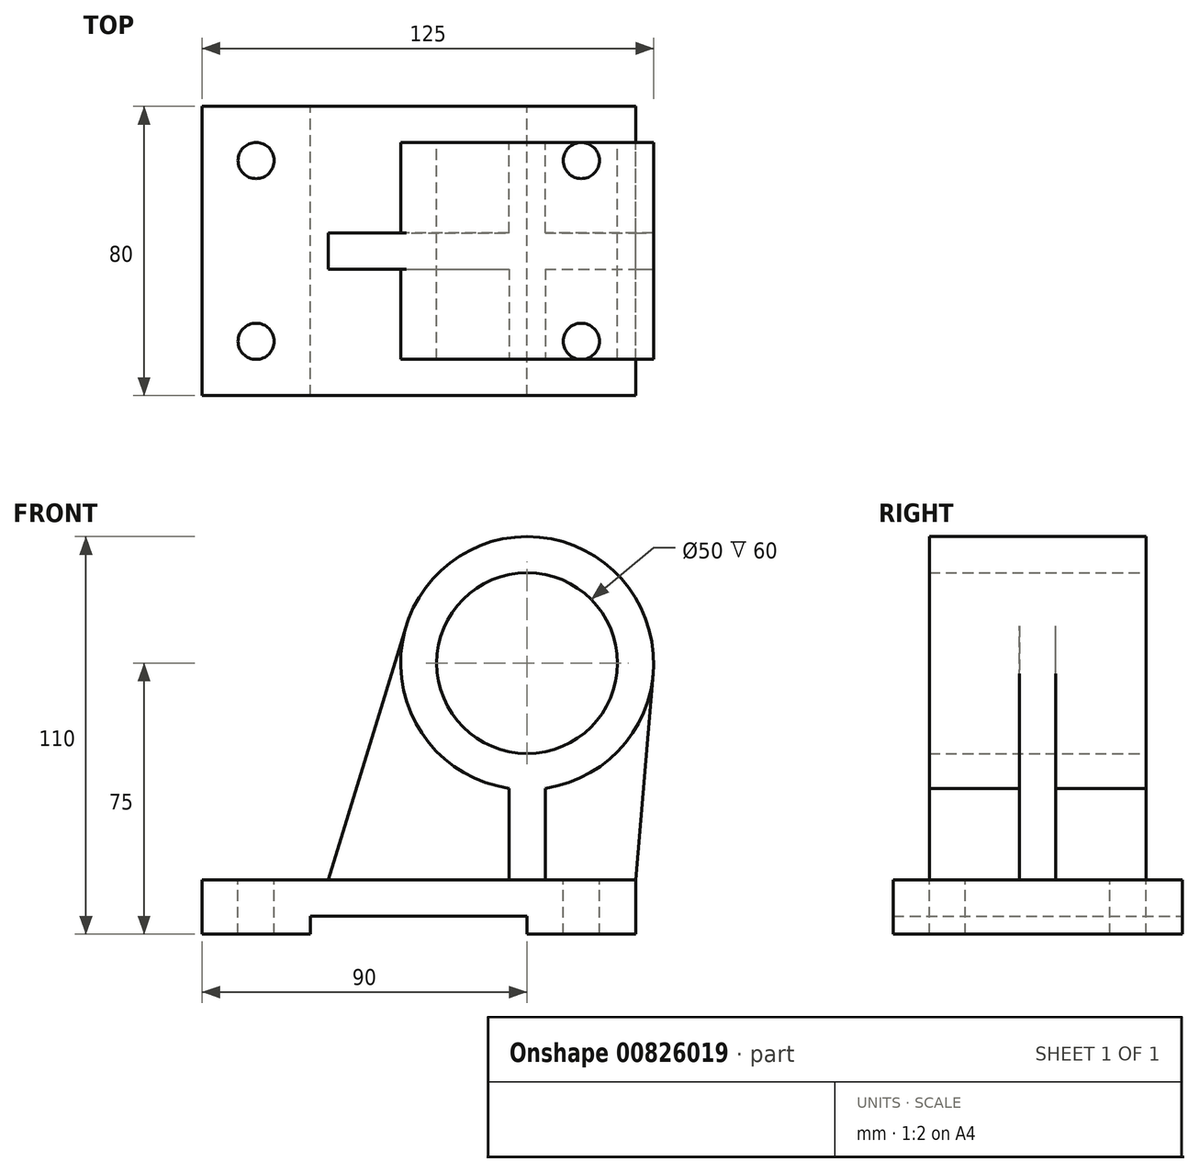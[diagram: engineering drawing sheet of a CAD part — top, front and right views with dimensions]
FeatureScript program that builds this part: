
annotation { "Feature Type Name" : "Feature", "Feature Type Description" : "" }
export const myFeature = defineFeature(function(context is Context, id is Id, definition is map)
    precondition{}
    {
        {
            var Q0;
            Q0=qCreatedBy(makeId("Front.planeOp"),FACE);
            var sketch = newSketch(context, id + "F0", { "sketchPlane" : qUnion([Q0])});
            skLineSegment(sketch, "E0", {"start": v(0, 0) * mm, "end": v(30, 0) * mm});
            skLineSegment(sketch, "E1", {"start": v(30, 0) * mm, "end": v(30, 5) * mm});
            skLineSegment(sketch, "E2", {"start": v(30, 5) * mm, "end": v(90, 5) * mm});
            skLineSegment(sketch, "E3", {"start": v(90, 5) * mm, "end": v(90, 0) * mm});
            skLineSegment(sketch, "E4", {"start": v(90, 0) * mm, "end": v(120, 0) * mm});
            skLineSegment(sketch, "E5", {"start": v(120, 0) * mm, "end": v(120, 15) * mm});
            skLineSegment(sketch, "E6", {"start": v(120, 15) * mm, "end": v(0, 15) * mm});
            skLineSegment(sketch, "E7", {"start": v(0, 15) * mm, "end": v(0, 0) * mm});
            skCircle(sketch, "E8", {"center": v(90, 75) * mm, "radius": 25 * mm});
            skCircle(sketch, "E9", {"center": v(90, 75) * mm, "radius": 35 * mm});
            skLineSegment(sketch, "E10", {"start": v(35, 15) * mm, "end": v(56.54, 85.26) * mm});
            skLineSegment(sketch, "E11", {"start": v(120, 15) * mm, "end": v(124.87, 72.02) * mm});
            skSolve(sketch);
        }
        {
            var Q0;
            Q0 = qSketchRegion(id + "F0", true);
            extrude(context, id + "F1", {"entities" : qUnion([Q0]), "endBound" : BoundingType.SYMMETRIC, "depth" : 80 * mm, "offsetDistance" : 25 * mm});
        }
        {
            var Q0;
            Q0=makeQuery(id+"F1.opExtrude","CAP_FACE",FACE,{"disambiguationData":[OSD([sQuery(id+"F0.wireOp",EDGE,"E0"),sQuery(id+"F0.wireOp",EDGE,"E1"),sQuery(id+"F0.wireOp",EDGE,"E2"),sQuery(id+"F0.wireOp",EDGE,"E3"),sQuery(id+"F0.wireOp",EDGE,"E4"),sQuery(id+"F0.wireOp",EDGE,"E5"),sQuery(id+"F0.wireOp",EDGE,"E6"),sQuery(id+"F0.wireOp",EDGE,"E7"),sQuery(id+"F0.wireOp",EDGE,"E8"),sQuery(id+"F0.wireOp",EDGE,"E9"),sQuery(id+"F0.wireOp",EDGE,"E10"),sQuery(id+"F0.wireOp",EDGE,"E11")])],"isStart":false});
            var sketch = newSketch(context, id + "F2", { "sketchPlane" : qUnion([Q0])});
            skLineSegment(sketch, "E12", {"start": v(35, 15) * mm, "end": v(120, 15) * mm});
            skSolve(sketch);
        }
        {
            var Q0;
            Q0=makeQuery(id+"F2.imprint","IMPRINT",FACE,{"disambiguationData":[TD([[makeQuery(id+"F2.imprint","IMPRINT",EDGE,{"derivedFrom":sQuery(id+"F2.wireOp",EDGE,"E12")}),1.0]])]});
            extrude(context, id + "F3", {"entities" : qUnion([Q0]), "operationType" : NewBodyOperationType.REMOVE, "oppositeDirection" : true, "depth" : 10 * mm, "offsetDistance" : 25 * mm});
        }
        {
            var Q0;
            Q0=makeQuery(id+"F1.opExtrude","CAP_FACE",FACE,{"disambiguationData":[OSD([sQuery(id+"F0.wireOp",EDGE,"E0"),sQuery(id+"F0.wireOp",EDGE,"E1"),sQuery(id+"F0.wireOp",EDGE,"E2"),sQuery(id+"F0.wireOp",EDGE,"E3"),sQuery(id+"F0.wireOp",EDGE,"E4"),sQuery(id+"F0.wireOp",EDGE,"E5"),sQuery(id+"F0.wireOp",EDGE,"E6"),sQuery(id+"F0.wireOp",EDGE,"E7"),sQuery(id+"F0.wireOp",EDGE,"E8"),sQuery(id+"F0.wireOp",EDGE,"E9"),sQuery(id+"F0.wireOp",EDGE,"E10"),sQuery(id+"F0.wireOp",EDGE,"E11")])],"isStart":true});
            var sketch = newSketch(context, id + "F4", { "sketchPlane" : qUnion([Q0])});
            skLineSegment(sketch, "E13", {"start": v(-35, 15) * mm, "end": v(-120, 15) * mm});
            skSolve(sketch);
        }
        {
            var Q0;
            Q0 = qSketchRegion(id + "F4", true);
            var Q1;
            Q1=makeQuery(id+"F4.imprint","IMPRINT",FACE,{"disambiguationData":[TD([[makeQuery(id+"F4.imprint","IMPRINT",EDGE,{"derivedFrom":sQuery(id+"F4.wireOp",EDGE,"E13")}),-1.0]])]});
            extrude(context, id + "F5", {"entities" : qUnion([Q0, Q1]), "operationType" : NewBodyOperationType.REMOVE, "oppositeDirection" : true, "depth" : 10 * mm, "offsetDistance" : 25 * mm});
        }
        {
            var Q0;
            Q0=makeQuery(id+"F3.boolean.opBoolean","COPY",FACE,{"derivedFrom":makeQuery(id+"F3.opExtrude","CAP_FACE",FACE,{"disambiguationData":[OSD([sQuery(id+"F0.wireOp",EDGE,"E8"),sQuery(id+"F0.wireOp",EDGE,"E9"),sQuery(id+"F0.wireOp",EDGE,"E10"),sQuery(id+"F0.wireOp",EDGE,"E11"),sQuery(id+"F2.wireOp",EDGE,"E12")])],"isStart":false})});
            var sketch = newSketch(context, id + "F6", { "sketchPlane" : qUnion([Q0])});
            skArc(sketch, "E14", {"start": v(56.54, 85.26) * mm, "mid": v(83.34, 40.64) * mm, "end": v(124.87, 72.02) * mm});
            skLineSegment(sketch, "E15", {"start": v(90, 75) * mm, "end": v(90, 15) * mm, "construction": true});
            skLineSegment(sketch, "E16", {"start": v(95, 15) * mm, "end": v(95, 40.36) * mm});
            skLineSegment(sketch, "E17", {"start": v(85, 15) * mm, "end": v(85, 40.36) * mm});
            skSolve(sketch);
        }
        {
            var Q0;
            Q0 = qSketchRegion(id + "F6", true);
            var Q1;
            {var subQ2=sQuery(id+"F6.wireOp",EDGE,"E17");Q1=makeQuery(id+"F6.imprint","IMPRINT",FACE,{"disambiguationData":[TD([[makeQuery(id+"F6.imprint","IMPRINT",EDGE,{"derivedFrom":subQ2}),1.0]])]});}
            var Q2;
            {var subQ2=sQuery(id+"F6.wireOp",EDGE,"E16");Q2=makeQuery(id+"F6.imprint","IMPRINT",FACE,{"disambiguationData":[TD([[makeQuery(id+"F6.imprint","IMPRINT",EDGE,{"derivedFrom":subQ2}),-1.0]])]});}
            extrude(context, id + "F7", {"entities" : qUnion([Q0, Q1, Q2]), "operationType" : NewBodyOperationType.REMOVE, "oppositeDirection" : true, "depth" : 25 * mm, "offsetDistance" : 25 * mm});
        }
        {
            var Q0;
            Q0=makeQuery(id+"F5.boolean.opBoolean","COPY",FACE,{"derivedFrom":makeQuery(id+"F5.opExtrude","CAP_FACE",FACE,{"disambiguationData":[OSD([sQuery(id+"F0.wireOp",EDGE,"E8"),sQuery(id+"F0.wireOp",EDGE,"E9"),sQuery(id+"F0.wireOp",EDGE,"E10"),sQuery(id+"F0.wireOp",EDGE,"E11"),sQuery(id+"F4.wireOp",EDGE,"E13")])],"isStart":false})});
            var sketch = newSketch(context, id + "F8", { "sketchPlane" : qUnion([Q0])});
            skLineSegment(sketch, "E18", {"start": v(-90, 75) * mm, "end": v(-90, 15) * mm, "construction": true});
            skArc(sketch, "E19", {"start": v(-56.54, 85.26) * mm, "mid": v(-83.34, 40.64) * mm, "end": v(-124.87, 72.02) * mm});
            skLineSegment(sketch, "E20", {"start": v(-95, 15) * mm, "end": v(-95, 40.36) * mm});
            skLineSegment(sketch, "E21", {"start": v(-85, 15) * mm, "end": v(-85, 40.36) * mm});
            skSolve(sketch);
        }
        {
            var Q0;
            Q0 = qSketchRegion(id + "F8", true);
            var Q1;
            {var subQ2=sQuery(id+"F8.wireOp",EDGE,"E20");Q1=makeQuery(id+"F8.imprint","IMPRINT",FACE,{"disambiguationData":[TD([[makeQuery(id+"F8.imprint","IMPRINT",EDGE,{"derivedFrom":subQ2}),1.0]])]});}
            var Q2;
            {var subQ2=sQuery(id+"F8.wireOp",EDGE,"E21");Q2=makeQuery(id+"F8.imprint","IMPRINT",FACE,{"disambiguationData":[TD([[makeQuery(id+"F8.imprint","IMPRINT",EDGE,{"derivedFrom":subQ2}),-1.0]])]});}
            extrude(context, id + "F9", {"entities" : qUnion([Q0, Q1, Q2]), "operationType" : NewBodyOperationType.REMOVE, "oppositeDirection" : true, "depth" : 25 * mm, "offsetDistance" : 25 * mm});
        }
        {
            var Q0;
            {var subQ0=sQuery(id+"F0.wireOp",EDGE,"E10");var subQ1=sQuery(id+"F4.wireOp",EDGE,"E13");var subQ2=makeQuery(id+"F5.boolean.opBoolean","COPY",EDGE,{"derivedFrom":makeQuery(id+"F5.opExtrude","CAP_EDGE",EDGE,{"disambiguationData":[OSD([subQ1])],"isStart":false})});var subQ3=sQuery(id+"F0.wireOp",EDGE,"E11");var subQ4=sQuery(id+"F2.wireOp",EDGE,"E12");var subQ5=makeQuery(id+"F3.boolean.opBoolean","COPY",EDGE,{"derivedFrom":makeQuery(id+"F3.opExtrude","CAP_EDGE",EDGE,{"disambiguationData":[OSD([subQ4])],"isStart":false})});Q0=makeQuery(id+"F9.boolean.opBoolean","MERGE",FACE,{"derivedFrom":[makeQuery(id+"F7.boolean.opBoolean","MERGE",FACE,{"derivedFrom":[makeQuery(id+"F5.boolean.opBoolean","MERGE",FACE,{"derivedFrom":[makeQuery(id+"F3.boolean.opBoolean","MERGE",FACE,{"derivedFrom":[makeQuery(id+"F1.opExtrude","SWEPT_FACE",FACE,{"disambiguationData":[OSD([sQuery(id+"F0.wireOp",EDGE,"E6")])]}),makeQuery(id+"F3.opExtrude","SWEPT_FACE",FACE,{"disambiguationData":[OSD([subQ4])]})]}),makeQuery(id+"F5.opExtrude","SWEPT_FACE",FACE,{"disambiguationData":[OSD([subQ1])]})]}),makeQuery(id+"F7.opExtrude","SWEPT_FACE",FACE,{"disambiguationData":[OSD([subQ4]),TDD([makeQuery(id+"F6.imprint","IMPRINT",EDGE,{"disambiguationData":[TD([[makeQuery(id+"F6.imprint","INTERSECT",VERTEX,{"derivedFrom":[subQ5,makeQuery(id+"F3.boolean.opBoolean","COPY",EDGE,{"derivedFrom":makeQuery(id+"F3.opExtrude","CAP_EDGE",EDGE,{"disambiguationData":[OSD([subQ3])],"isStart":false})})]}),1.0]])],"derivedFrom":subQ5})])]}),makeQuery(id+"F7.opExtrude","SWEPT_FACE",FACE,{"disambiguationData":[OSD([subQ4]),TDD([makeQuery(id+"F6.imprint","IMPRINT",EDGE,{"disambiguationData":[TD([[makeQuery(id+"F6.imprint","INTERSECT",VERTEX,{"derivedFrom":[subQ5,makeQuery(id+"F3.boolean.opBoolean","COPY",EDGE,{"derivedFrom":makeQuery(id+"F3.opExtrude","CAP_EDGE",EDGE,{"disambiguationData":[OSD([subQ0])],"isStart":false})})]}),-1.0]])],"derivedFrom":subQ5})])]})]}),makeQuery(id+"F9.opExtrude","SWEPT_FACE",FACE,{"disambiguationData":[OSD([subQ1]),TDD([makeQuery(id+"F8.imprint","IMPRINT",EDGE,{"disambiguationData":[TD([[makeQuery(id+"F8.imprint","INTERSECT",VERTEX,{"derivedFrom":[subQ2,makeQuery(id+"F5.boolean.opBoolean","COPY",EDGE,{"derivedFrom":makeQuery(id+"F5.opExtrude","CAP_EDGE",EDGE,{"disambiguationData":[OSD([subQ3])],"isStart":false})})]}),1.0]])],"derivedFrom":subQ2})])]}),makeQuery(id+"F9.opExtrude","SWEPT_FACE",FACE,{"disambiguationData":[OSD([subQ1]),TDD([makeQuery(id+"F8.imprint","IMPRINT",EDGE,{"disambiguationData":[TD([[makeQuery(id+"F8.imprint","INTERSECT",VERTEX,{"derivedFrom":[subQ2,makeQuery(id+"F5.boolean.opBoolean","COPY",EDGE,{"derivedFrom":makeQuery(id+"F5.opExtrude","CAP_EDGE",EDGE,{"disambiguationData":[OSD([subQ0])],"isStart":false})})]}),-1.0]])],"derivedFrom":subQ2})])]})]});}
            var sketch = newSketch(context, id + "F10", { "sketchPlane" : qUnion([Q0])});
            skLineSegment(sketch, "E22", {"start": v(0, -25) * mm, "end": v(120, -25) * mm, "construction": true});
            skLineSegment(sketch, "E23", {"start": v(15, -40) * mm, "end": v(15, 40) * mm, "construction": true});
            skLineSegment(sketch, "E24", {"start": v(0, 25) * mm, "end": v(120, 25) * mm, "construction": true});
            skLineSegment(sketch, "E25", {"start": v(105, -40) * mm, "end": v(105, 40) * mm, "construction": true});
            skLineSegment(sketch, "E26", {"start": v(60, 40) * mm, "end": v(60, -40) * mm, "construction": true});
            skPoint(sketch, "E27", {"position": v(15, 25) * mm});
            skPoint(sketch, "E28", {"position": v(15, -25) * mm});
            skPoint(sketch, "E29", {"position": v(105, -25) * mm});
            skPoint(sketch, "E30", {"position": v(105, 25) * mm});
            skSolve(sketch);
        }
        {
            var Q0;
            Q0=sQuery(id+"F10.wireOp",VERTEX,"E27");
            var Q1;
            Q1=sQuery(id+"F10.wireOp",VERTEX,"E28");
            var Q2;
            Q2=sQuery(id+"F10.wireOp",VERTEX,"E29");
            var Q3;
            Q3=sQuery(id+"F10.wireOp",VERTEX,"E30");
            var Q4;
            Q4=makeQuery(id+"F1.opExtrude","SWEPT_BODY",BODY,{"disambiguationData":[OSD([sQuery(id+"F0.wireOp",EDGE,"E0"),sQuery(id+"F0.wireOp",EDGE,"E1"),sQuery(id+"F0.wireOp",EDGE,"E2"),sQuery(id+"F0.wireOp",EDGE,"E3"),sQuery(id+"F0.wireOp",EDGE,"E4"),sQuery(id+"F0.wireOp",EDGE,"E5"),sQuery(id+"F0.wireOp",EDGE,"E6"),sQuery(id+"F0.wireOp",EDGE,"E7"),sQuery(id+"F0.wireOp",EDGE,"E8"),sQuery(id+"F0.wireOp",EDGE,"E9"),sQuery(id+"F0.wireOp",EDGE,"E10"),sQuery(id+"F0.wireOp",EDGE,"E11")])]});
            hole(context, id + "F11", {"style" : HoleStyle.SIMPLE, "endStyle" : HoleEndStyle.BLIND, "holeDiameter" : 10 * mm, "majorDiameter" : 10 * mm, "holeDepth" : 16.5 * mm, "isTappedThrough" : true, "tappedDepth" : 12 * mm, "tapClearance" : 3, "startFromSketch" : true, "locations" : qUnion([Q0, Q1, Q2, Q3]), "scope" : qUnion([Q4])});
        }
    });
